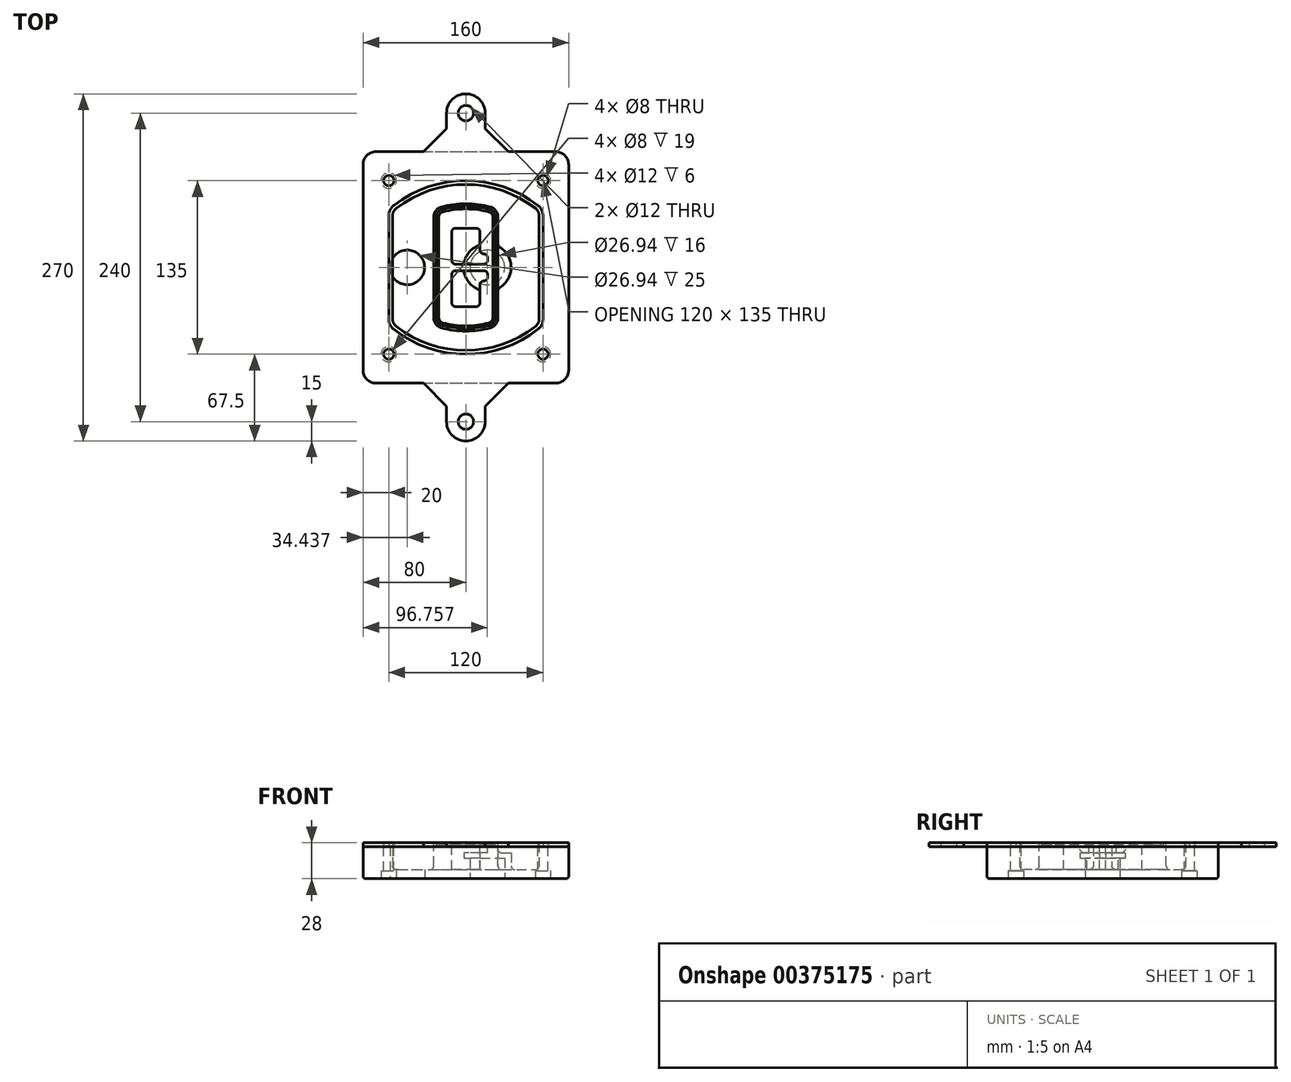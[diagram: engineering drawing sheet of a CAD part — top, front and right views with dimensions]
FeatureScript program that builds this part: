
annotation { "Feature Type Name" : "Feature", "Feature Type Description" : "" }
export const myFeature = defineFeature(function(context is Context, id is Id, definition is map)
    precondition{}
    {
        {
            var Q0;
            Q0=qCreatedBy(makeId("Top.planeOp"),FACE);
            var sketch = newSketch(context, id + "F0", { "sketchPlane" : qUnion([Q0])});
            skPoint(sketch, "E0.rect.middle", {"position": v(0, 0) * mm});
            skLineSegment(sketch, "E1.bottom", {"start": v(-70, -90) * mm, "end": v(70, -90) * mm});
            skLineSegment(sketch, "E1.top", {"start": v(-70, 90) * mm, "end": v(70, 90) * mm});
            skLineSegment(sketch, "E1.left", {"start": v(-80, -80) * mm, "end": v(-80, 80) * mm});
            skLineSegment(sketch, "E1.right", {"start": v(80, -80) * mm, "end": v(80, 80) * mm});
            skLineSegment(sketch, "E2", {"start": v(-80, 90) * mm, "end": v(80, -90) * mm, "construction": true});
            skLineSegment(sketch, "E3", {"start": v(80, 90) * mm, "end": v(-80, -90) * mm, "construction": true});
            skCircle(sketch, "E4", {"center": v(-60, 67.5) * mm, "radius": 4 * mm});
            skCircle(sketch, "E5", {"center": v(60, 67.5) * mm, "radius": 4 * mm});
            skCircle(sketch, "E6", {"center": v(60, -67.5) * mm, "radius": 4 * mm});
            skCircle(sketch, "E7", {"center": v(-60, -67.5) * mm, "radius": 4 * mm});
            skLineSegment(sketch, "E8", {"start": v(-60, 67.5) * mm, "end": v(60, 67.5) * mm, "construction": true});
            skLineSegment(sketch, "E9", {"start": v(60, 67.5) * mm, "end": v(60, -67.5) * mm, "construction": true});
            skLineSegment(sketch, "E10", {"start": v(60, -67.5) * mm, "end": v(-60, -67.5) * mm, "construction": true});
            skLineSegment(sketch, "E11", {"start": v(-60, -67.5) * mm, "end": v(-60, 67.5) * mm, "construction": true});
            skLineSegment(sketch, "E12", {"start": v(-60, 40.3) * mm, "end": v(-60, -40.3) * mm});
            skLineSegment(sketch, "E13", {"start": v(60, 40.3) * mm, "end": v(60, -40.3) * mm});
            skArc(sketch, "E14", {"start": v(56.15, 48.18) * mm, "mid": v(0, 67.5) * mm, "end": v(-56.15, 48.18) * mm});
            skArc(sketch, "E15", {"start": v(-56.15, -48.18) * mm, "mid": v(0, -67.5) * mm, "end": v(56.15, -48.18) * mm});
            skLineSegment(sketch, "E16", {"start": v(-60, 0) * mm, "end": v(60, 0) * mm, "construction": true});
            skPoint(sketch, "E17.visualSharp", {"position": v(-60, -45) * mm});
            skArc(sketch, "E17.filletArc", {"start": v(-60, -40.3) * mm, "mid": v(-58.99, -44.68) * mm, "end": v(-56.15, -48.18) * mm});
            skPoint(sketch, "E18.visualSharp", {"position": v(-60, 45) * mm});
            skArc(sketch, "E18.filletArc", {"start": v(-56.15, 48.18) * mm, "mid": v(-58.99, 44.68) * mm, "end": v(-60, 40.3) * mm});
            skPoint(sketch, "E19.visualSharp", {"position": v(60, 45) * mm});
            skArc(sketch, "E19.filletArc", {"start": v(60, 40.3) * mm, "mid": v(58.99, 44.68) * mm, "end": v(56.15, 48.18) * mm});
            skPoint(sketch, "E20.visualSharp", {"position": v(60, -45) * mm});
            skArc(sketch, "E20.filletArc", {"start": v(56.15, -48.18) * mm, "mid": v(58.99, -44.68) * mm, "end": v(60, -40.3) * mm});
            skPoint(sketch, "E21.visualSharp", {"position": v(-80, 90) * mm});
            skArc(sketch, "E21.filletArc", {"start": v(-70, 90) * mm, "mid": v(-77.07, 87.07) * mm, "end": v(-80, 80) * mm});
            skPoint(sketch, "E22.visualSharp", {"position": v(80, 90) * mm});
            skArc(sketch, "E22.filletArc", {"start": v(80, 80) * mm, "mid": v(77.07, 87.07) * mm, "end": v(70, 90) * mm});
            skPoint(sketch, "E23.visualSharp", {"position": v(80, -90) * mm});
            skArc(sketch, "E23.filletArc", {"start": v(70, -90) * mm, "mid": v(77.07, -87.07) * mm, "end": v(80, -80) * mm});
            skPoint(sketch, "E24.visualSharp", {"position": v(-80, -90) * mm});
            skArc(sketch, "E24.filletArc", {"start": v(-80, -80) * mm, "mid": v(-77.07, -87.07) * mm, "end": v(-70, -90) * mm});
            skArc(sketch, "E25.0", {"start": v(57, 40.3) * mm, "mid": v(56.3, 43.36) * mm, "end": v(54.3, 45.81) * mm});
            skLineSegment(sketch, "E25.1", {"start": v(57, 40.3) * mm, "end": v(57, -40.3) * mm});
            skArc(sketch, "E25.2", {"start": v(54.3, -45.81) * mm, "mid": v(56.3, -43.36) * mm, "end": v(57, -40.3) * mm});
            skArc(sketch, "E25.3", {"start": v(-54.3, -45.81) * mm, "mid": v(0, -64.5) * mm, "end": v(54.3, -45.81) * mm});
            skArc(sketch, "E25.4", {"start": v(-57, -40.3) * mm, "mid": v(-56.3, -43.36) * mm, "end": v(-54.3, -45.81) * mm});
            skArc(sketch, "E25.5", {"start": v(54.3, 45.81) * mm, "mid": v(0, 64.5) * mm, "end": v(-54.3, 45.81) * mm});
            skLineSegment(sketch, "E25.6", {"start": v(-57, 40.3) * mm, "end": v(-57, -40.3) * mm});
            skArc(sketch, "E25.7", {"start": v(-54.3, 45.81) * mm, "mid": v(-56.3, 43.36) * mm, "end": v(-57, 40.3) * mm});
            skArc(sketch, "E26.0", {"start": v(-58.62, 51.33) * mm, "mid": v(-62.58, 46.43) * mm, "end": v(-64, 40.3) * mm});
            skArc(sketch, "E26.1", {"start": v(58.62, 51.33) * mm, "mid": v(0, 71.5) * mm, "end": v(-58.62, 51.33) * mm});
            skArc(sketch, "E26.2", {"start": v(64, 40.3) * mm, "mid": v(62.58, 46.43) * mm, "end": v(58.62, 51.33) * mm});
            skLineSegment(sketch, "E26.3", {"start": v(64, 40.3) * mm, "end": v(64, -40.3) * mm});
            skArc(sketch, "E26.4", {"start": v(58.62, -51.33) * mm, "mid": v(62.58, -46.43) * mm, "end": v(64, -40.3) * mm});
            skLineSegment(sketch, "E26.5", {"start": v(-64, 40.3) * mm, "end": v(-64, -40.3) * mm});
            skArc(sketch, "E26.6", {"start": v(-58.62, -51.33) * mm, "mid": v(0, -71.5) * mm, "end": v(58.62, -51.33) * mm});
            skArc(sketch, "E26.7", {"start": v(-64, -40.3) * mm, "mid": v(-62.58, -46.43) * mm, "end": v(-58.62, -51.33) * mm});
            skSolve(sketch);
        }
        {
            var Q0;
            Q0=makeQuery(id+"F0.imprint","IMPRINT",FACE,{"disambiguationData":[TD([[makeQuery(id+"F0.imprint","IMPRINT",EDGE,{"derivedFrom":sQuery(id+"F0.wireOp",EDGE,"E1.bottom")}),1.0]])]});
            var Q1;
            Q1=makeQuery(id+"F0.imprint","IMPRINT",FACE,{"disambiguationData":[TD([[makeQuery(id+"F0.imprint","IMPRINT",EDGE,{"derivedFrom":sQuery(id+"F0.wireOp",EDGE,"E12")}),1.0]])]});
            var Q2;
            Q2=makeQuery(id+"F0.imprint","IMPRINT",FACE,{"disambiguationData":[TD([[makeQuery(id+"F0.imprint","IMPRINT",EDGE,{"derivedFrom":sQuery(id+"F0.wireOp",EDGE,"E25.0")}),1.0]])]});
            var Q3;
            Q3=makeQuery(id+"F0.imprint","IMPRINT",FACE,{"disambiguationData":[TD([[makeQuery(id+"F0.imprint","IMPRINT",EDGE,{"derivedFrom":sQuery(id+"F0.wireOp",EDGE,"E12")}),-1.0]])]});
            extrude(context, id + "F1", {"entities" : qUnion([Q0, Q1, Q2, Q3]), "oppositeDirection" : true, "depth" : 25 * mm});
        }
        {
            var Q0;
            Q0=makeQuery(id+"F0.imprint","IMPRINT",FACE,{"disambiguationData":[TD([[makeQuery(id+"F0.imprint","IMPRINT",EDGE,{"derivedFrom":sQuery(id+"F0.wireOp",EDGE,"E12")}),1.0]])]});
            extrude(context, id + "F2", {"entities" : qUnion([Q0]), "operationType" : NewBodyOperationType.ADD, "depth" : 3 * mm});
        }
        {
            var Q0;
            Q0=makeQuery(id+"F0.imprint","IMPRINT",FACE,{"disambiguationData":[TD([[makeQuery(id+"F0.imprint","IMPRINT",EDGE,{"derivedFrom":sQuery(id+"F0.wireOp",EDGE,"E25.0")}),1.0]])]});
            extrude(context, id + "F3", {"entities" : qUnion([Q0]), "operationType" : NewBodyOperationType.REMOVE, "oppositeDirection" : true, "depth" : 18 * mm});
        }
        {
            var Q0;
            Q0=makeQuery(id+"F2.opExtrude","CAP_FACE",FACE,{"disambiguationData":[OSD([sQuery(id+"F0.wireOp",EDGE,"E12"),sQuery(id+"F0.wireOp",EDGE,"E13"),sQuery(id+"F0.wireOp",EDGE,"E14"),sQuery(id+"F0.wireOp",EDGE,"E15"),sQuery(id+"F0.wireOp",EDGE,"E17.filletArc"),sQuery(id+"F0.wireOp",EDGE,"E18.filletArc"),sQuery(id+"F0.wireOp",EDGE,"E19.filletArc"),sQuery(id+"F0.wireOp",EDGE,"E20.filletArc"),sQuery(id+"F0.wireOp",EDGE,"E25.0"),sQuery(id+"F0.wireOp",EDGE,"E25.1"),sQuery(id+"F0.wireOp",EDGE,"E25.2"),sQuery(id+"F0.wireOp",EDGE,"E25.3"),sQuery(id+"F0.wireOp",EDGE,"E25.4"),sQuery(id+"F0.wireOp",EDGE,"E25.5"),sQuery(id+"F0.wireOp",EDGE,"E25.6"),sQuery(id+"F0.wireOp",EDGE,"E25.7")])],"isStart":false});
            var sketch = newSketch(context, id + "F4", { "sketchPlane" : qUnion([Q0])});
            skArc(sketch, "E27.0", {"start": v(-19.08, -46.97) * mm, "mid": v(0, -49.5) * mm, "end": v(19.08, -46.97) * mm});
            skArc(sketch, "E28.0", {"start": v(19.08, 46.97) * mm, "mid": v(0, 49.5) * mm, "end": v(-19.08, 46.97) * mm});
            skLineSegment(sketch, "E29", {"start": v(-25, 39.25) * mm, "end": v(-25, -39.25) * mm});
            skLineSegment(sketch, "E30", {"start": v(25, 39.25) * mm, "end": v(25, -39.25) * mm});
            skLineSegment(sketch, "E31", {"start": v(-25, 45.1) * mm, "end": v(25, 45.1) * mm, "construction": true});
            skLineSegment(sketch, "E32", {"start": v(-25, -45.1) * mm, "end": v(25, -45.1) * mm, "construction": true});
            skPoint(sketch, "E33.visualSharp", {"position": v(-25, 45.1) * mm});
            skArc(sketch, "E33.filletArc", {"start": v(-19.08, 46.97) * mm, "mid": v(-23.35, 44.11) * mm, "end": v(-25, 39.25) * mm});
            skPoint(sketch, "E34.visualSharp", {"position": v(25, 45.1) * mm});
            skArc(sketch, "E34.filletArc", {"start": v(25, 39.25) * mm, "mid": v(23.35, 44.11) * mm, "end": v(19.08, 46.97) * mm});
            skPoint(sketch, "E35.visualSharp", {"position": v(25, -45.1) * mm});
            skArc(sketch, "E35.filletArc", {"start": v(19.08, -46.97) * mm, "mid": v(23.35, -44.11) * mm, "end": v(25, -39.25) * mm});
            skPoint(sketch, "E36.visualSharp", {"position": v(-25, -45.1) * mm});
            skArc(sketch, "E36.filletArc", {"start": v(-25, -39.25) * mm, "mid": v(-23.35, -44.11) * mm, "end": v(-19.08, -46.97) * mm});
            skArc(sketch, "E37.0", {"start": v(54.3, 45.81) * mm, "mid": v(0, 64.5) * mm, "end": v(-54.3, 45.81) * mm});
            skArc(sketch, "E37.1", {"start": v(-54.3, 45.81) * mm, "mid": v(-56.3, 43.36) * mm, "end": v(-57, 40.3) * mm});
            skLineSegment(sketch, "E37.2", {"start": v(-57, 40.3) * mm, "end": v(-57, -40.3) * mm});
            skArc(sketch, "E37.3", {"start": v(-57, -40.3) * mm, "mid": v(-56.3, -43.36) * mm, "end": v(-54.3, -45.81) * mm});
            skArc(sketch, "E37.4", {"start": v(-54.3, -45.81) * mm, "mid": v(0, -64.5) * mm, "end": v(54.3, -45.81) * mm});
            skArc(sketch, "E37.5", {"start": v(54.3, -45.81) * mm, "mid": v(56.3, -43.36) * mm, "end": v(57, -40.3) * mm});
            skLineSegment(sketch, "E37.6", {"start": v(57, 40.3) * mm, "end": v(57, -40.3) * mm});
            skArc(sketch, "E37.7", {"start": v(57, 40.3) * mm, "mid": v(56.3, 43.36) * mm, "end": v(54.3, 45.81) * mm});
            skLineSegment(sketch, "E38.0", {"start": v(23, 39.25) * mm, "end": v(23, -39.25) * mm});
            skArc(sketch, "E38.1", {"start": v(18.56, -45.04) * mm, "mid": v(21.76, -42.9) * mm, "end": v(23, -39.25) * mm});
            skArc(sketch, "E38.2", {"start": v(-18.56, -45.04) * mm, "mid": v(0, -47.5) * mm, "end": v(18.56, -45.04) * mm});
            skArc(sketch, "E38.3", {"start": v(-23, -39.25) * mm, "mid": v(-21.76, -42.9) * mm, "end": v(-18.56, -45.04) * mm});
            skLineSegment(sketch, "E38.4", {"start": v(-23, 39.25) * mm, "end": v(-23, -39.25) * mm});
            skArc(sketch, "E38.5", {"start": v(23, 39.25) * mm, "mid": v(21.76, 42.9) * mm, "end": v(18.56, 45.04) * mm});
            skArc(sketch, "E38.6", {"start": v(-18.56, 45.04) * mm, "mid": v(-21.76, 42.9) * mm, "end": v(-23, 39.25) * mm});
            skArc(sketch, "E38.7", {"start": v(18.56, 45.04) * mm, "mid": v(0, 47.5) * mm, "end": v(-18.56, 45.04) * mm});
            skArc(sketch, "E39.0", {"start": v(21, 39.25) * mm, "mid": v(20.18, 41.68) * mm, "end": v(18.04, 43.1) * mm});
            skLineSegment(sketch, "E39.1", {"start": v(21, 39.25) * mm, "end": v(21, -39.25) * mm});
            skArc(sketch, "E39.2", {"start": v(18.04, -43.1) * mm, "mid": v(20.18, -41.68) * mm, "end": v(21, -39.25) * mm});
            skArc(sketch, "E39.3", {"start": v(-18.04, -43.1) * mm, "mid": v(0, -45.5) * mm, "end": v(18.04, -43.1) * mm});
            skArc(sketch, "E39.4", {"start": v(-21, -39.25) * mm, "mid": v(-20.18, -41.68) * mm, "end": v(-18.04, -43.1) * mm});
            skArc(sketch, "E39.5", {"start": v(18.04, 43.1) * mm, "mid": v(0, 45.5) * mm, "end": v(-18.04, 43.1) * mm});
            skLineSegment(sketch, "E39.6", {"start": v(-21, 39.25) * mm, "end": v(-21, -39.25) * mm});
            skArc(sketch, "E39.7", {"start": v(-18.04, 43.1) * mm, "mid": v(-20.18, 41.68) * mm, "end": v(-21, 39.25) * mm});
            skLineSegment(sketch, "E40", {"start": v(-25, 0) * mm, "end": v(25, 0) * mm, "construction": true});
            skLineSegment(sketch, "E41", {"start": v(-11, 5.5) * mm, "end": v(-11, 27.5) * mm});
            skLineSegment(sketch, "E42", {"start": v(-8, 30.5) * mm, "end": v(8, 30.5) * mm});
            skLineSegment(sketch, "E43", {"start": v(11, 27.5) * mm, "end": v(11, 13.5) * mm});
            skLineSegment(sketch, "E44", {"start": v(14, 10.5) * mm, "end": v(14, 10.5) * mm});
            skLineSegment(sketch, "E45", {"start": v(17, 7.5) * mm, "end": v(17, 5.5) * mm});
            skLineSegment(sketch, "E46", {"start": v(14, 2.5) * mm, "end": v(-8, 2.5) * mm});
            skPoint(sketch, "E47.visualSharp", {"position": v(-11, 30.5) * mm});
            skArc(sketch, "E47.filletArc", {"start": v(-8, 30.5) * mm, "mid": v(-10.12, 29.62) * mm, "end": v(-11, 27.5) * mm});
            skPoint(sketch, "E48.visualSharp", {"position": v(11, 30.5) * mm});
            skArc(sketch, "E48.filletArc", {"start": v(11, 27.5) * mm, "mid": v(10.12, 29.62) * mm, "end": v(8, 30.5) * mm});
            skPoint(sketch, "E49.visualSharp", {"position": v(11, 10.5) * mm});
            skArc(sketch, "E49.filletArc", {"start": v(11, 13.5) * mm, "mid": v(11.88, 11.38) * mm, "end": v(14, 10.5) * mm});
            skPoint(sketch, "E50.visualSharp", {"position": v(17, 10.5) * mm});
            skArc(sketch, "E50.filletArc", {"start": v(17, 7.5) * mm, "mid": v(16.12, 9.62) * mm, "end": v(14, 10.5) * mm});
            skPoint(sketch, "E51.visualSharp", {"position": v(17, 2.5) * mm});
            skArc(sketch, "E51.filletArc", {"start": v(14, 2.5) * mm, "mid": v(16.12, 3.38) * mm, "end": v(17, 5.5) * mm});
            skPoint(sketch, "E52.visualSharp", {"position": v(-11, 2.5) * mm});
            skArc(sketch, "E52.filletArc", {"start": v(-11, 5.5) * mm, "mid": v(-10.12, 3.38) * mm, "end": v(-8, 2.5) * mm});
            skLineSegment(sketch, "E53.0.MirrorCS", {"start": v(14, -2.5) * mm, "end": v(-8, -2.5) * mm});
            skArc(sketch, "E54.0.MirrorCS", {"start": v(-11, -5.5) * mm, "mid": v(-10.12, -3.38) * mm, "end": v(-8, -2.5) * mm});
            skLineSegment(sketch, "E55.0.MirrorCS", {"start": v(-11, -5.5) * mm, "end": v(-11, -27.5) * mm});
            skArc(sketch, "E56.0.MirrorCS", {"start": v(-8, -30.5) * mm, "mid": v(-10.12, -29.62) * mm, "end": v(-11, -27.5) * mm});
            skLineSegment(sketch, "E57.0.MirrorCS", {"start": v(-8, -30.5) * mm, "end": v(8, -30.5) * mm});
            skArc(sketch, "E58.0.MirrorCS", {"start": v(11, -27.5) * mm, "mid": v(10.12, -29.62) * mm, "end": v(8, -30.5) * mm});
            skLineSegment(sketch, "E59.0.MirrorCS", {"start": v(11, -27.5) * mm, "end": v(11, -13.5) * mm});
            skArc(sketch, "E60.0.MirrorCS", {"start": v(11, -13.5) * mm, "mid": v(11.88, -11.38) * mm, "end": v(14, -10.5) * mm});
            skArc(sketch, "E61.0.MirrorCS", {"start": v(17, -7.5) * mm, "mid": v(16.12, -9.62) * mm, "end": v(14, -10.5) * mm});
            skLineSegment(sketch, "E62.0.MirrorCS", {"start": v(17, -7.5) * mm, "end": v(17, -5.5) * mm});
            skArc(sketch, "E63.0.MirrorCS", {"start": v(14, -2.5) * mm, "mid": v(16.12, -3.38) * mm, "end": v(17, -5.5) * mm});
            skSolve(sketch);
        }
        {
            var Q0;
            Q0=makeQuery(id+"F4.imprint","IMPRINT",FACE,{"disambiguationData":[TD([[makeQuery(id+"F4.imprint","IMPRINT",EDGE,{"derivedFrom":sQuery(id+"F4.wireOp",EDGE,"E27.0")}),1.0]])]});
            var Q1;
            Q1=makeQuery(id+"F4.imprint","IMPRINT",FACE,{"disambiguationData":[TD([[makeQuery(id+"F4.imprint","IMPRINT",EDGE,{"derivedFrom":sQuery(id+"F4.wireOp",EDGE,"E38.0")}),-1.0]])]});
            var Q2;
            Q2=makeQuery(id+"F4.imprint","IMPRINT",FACE,{"disambiguationData":[TD([[makeQuery(id+"F4.imprint","IMPRINT",EDGE,{"derivedFrom":sQuery(id+"F4.wireOp",EDGE,"E39.0")}),1.0]])]});
            extrude(context, id + "F5", {"entities" : qUnion([Q0, Q1, Q2]), "operationType" : NewBodyOperationType.ADD, "endBound" : BoundingType.UP_TO_NEXT, "oppositeDirection" : true, "depth" : 25 * mm});
        }
        {
            var Q0;
            Q0=makeQuery(id+"F4.imprint","IMPRINT",FACE,{"disambiguationData":[TD([[makeQuery(id+"F4.imprint","IMPRINT",EDGE,{"derivedFrom":sQuery(id+"F4.wireOp",EDGE,"E38.0")}),-1.0]])]});
            extrude(context, id + "F6", {"entities" : qUnion([Q0]), "operationType" : NewBodyOperationType.REMOVE, "oppositeDirection" : true, "depth" : 2 * mm});
        }
        {
            var Q0;
            Q0=makeQuery(id+"F1.opExtrude","CAP_FACE",FACE,{"disambiguationData":[OSD([sQuery(id+"F0.wireOp",EDGE,"E1.bottom"),sQuery(id+"F0.wireOp",EDGE,"E1.top"),sQuery(id+"F0.wireOp",EDGE,"E1.left"),sQuery(id+"F0.wireOp",EDGE,"E1.right"),sQuery(id+"F0.wireOp",EDGE,"E4"),sQuery(id+"F0.wireOp",EDGE,"E5"),sQuery(id+"F0.wireOp",EDGE,"E6"),sQuery(id+"F0.wireOp",EDGE,"E7"),sQuery(id+"F0.wireOp",EDGE,"E21.filletArc"),sQuery(id+"F0.wireOp",EDGE,"E22.filletArc"),sQuery(id+"F0.wireOp",EDGE,"E23.filletArc"),sQuery(id+"F0.wireOp",EDGE,"E24.filletArc")])],"isStart":false});
            var sketch = newSketch(context, id + "F7", { "sketchPlane" : qUnion([Q0])});
            skCircle(sketch, "E64", {"center": v(16.76, 0) * mm, "radius": 13.47 * mm});
            skCircle(sketch, "E65", {"center": v(-45.56, 0) * mm, "radius": 13.47 * mm});
            skLineSegment(sketch, "E66", {"start": v(80, 0) * mm, "end": v(-80, 0) * mm});
            skCircle(sketch, "E67", {"center": v(16.76, 0) * mm, "radius": 18.47 * mm});
            skCircle(sketch, "E68", {"center": v(60, -67.5) * mm, "radius": 6 * mm});
            skCircle(sketch, "E69", {"center": v(-60, -67.5) * mm, "radius": 6 * mm});
            skCircle(sketch, "E70", {"center": v(-60, 67.5) * mm, "radius": 6 * mm});
            skCircle(sketch, "E71", {"center": v(60, 67.5) * mm, "radius": 6 * mm});
            skSolve(sketch);
        }
        {
            var Q0;
            {var subQ1=sQuery(id+"F7.wireOp",EDGE,"E66");var subQ4=sQuery(id+"F7.wireOp",EDGE,"E64");var subQ6=makeQuery(id+"F7.imprint","INTERSECT",VERTEX,{"disambiguationData":[OD(0.0)],"derivedFrom":[subQ4,subQ1]});Q0=makeQuery(id+"F7.imprint","IMPRINT",FACE,{"disambiguationData":[TD([[makeQuery(id+"F7.imprint","IMPRINT",EDGE,{"disambiguationData":[TD([[subQ6,-1.0]])],"derivedFrom":subQ4}),-1.0]])]});}
            var Q1;
            {var subQ0=sQuery(id+"F7.wireOp",EDGE,"E66");var subQ1=sQuery(id+"F7.wireOp",EDGE,"E64");var subQ3=makeQuery(id+"F7.imprint","INTERSECT",VERTEX,{"disambiguationData":[OD(0.0)],"derivedFrom":[subQ1,subQ0]});Q1=makeQuery(id+"F7.imprint","IMPRINT",FACE,{"disambiguationData":[TD([[makeQuery(id+"F7.imprint","IMPRINT",EDGE,{"disambiguationData":[TD([[subQ3,-1.0]])],"derivedFrom":subQ1}),1.0]])]});}
            var Q2;
            {var subQ0=sQuery(id+"F7.wireOp",EDGE,"E66");var subQ1=sQuery(id+"F7.wireOp",EDGE,"E64");var subQ3=makeQuery(id+"F7.imprint","INTERSECT",VERTEX,{"disambiguationData":[OD(0.0)],"derivedFrom":[subQ1,subQ0]});Q2=makeQuery(id+"F7.imprint","IMPRINT",FACE,{"disambiguationData":[TD([[makeQuery(id+"F7.imprint","IMPRINT",EDGE,{"disambiguationData":[TD([[subQ3,1.0]])],"derivedFrom":subQ1}),1.0]])]});}
            var Q3;
            {var subQ1=sQuery(id+"F7.wireOp",EDGE,"E66");var subQ4=sQuery(id+"F7.wireOp",EDGE,"E64");var subQ6=makeQuery(id+"F7.imprint","INTERSECT",VERTEX,{"disambiguationData":[OD(0.0)],"derivedFrom":[subQ4,subQ1]});Q3=makeQuery(id+"F7.imprint","IMPRINT",FACE,{"disambiguationData":[TD([[makeQuery(id+"F7.imprint","IMPRINT",EDGE,{"disambiguationData":[TD([[subQ6,1.0]])],"derivedFrom":subQ4}),-1.0]])]});}
            extrude(context, id + "F8", {"entities" : qUnion([Q0, Q1, Q2, Q3]), "operationType" : NewBodyOperationType.ADD, "oppositeDirection" : true, "depth" : 20 * mm});
        }
        {
            var Q0;
            {var subQ0=sQuery(id+"F7.wireOp",EDGE,"E66");var subQ1=sQuery(id+"F7.wireOp",EDGE,"E64");var subQ3=makeQuery(id+"F7.imprint","INTERSECT",VERTEX,{"disambiguationData":[OD(0.0)],"derivedFrom":[subQ1,subQ0]});Q0=makeQuery(id+"F7.imprint","IMPRINT",FACE,{"disambiguationData":[TD([[makeQuery(id+"F7.imprint","IMPRINT",EDGE,{"disambiguationData":[TD([[subQ3,-1.0]])],"derivedFrom":subQ1}),1.0]])]});}
            var Q1;
            {var subQ0=sQuery(id+"F7.wireOp",EDGE,"E66");var subQ1=sQuery(id+"F7.wireOp",EDGE,"E64");var subQ3=makeQuery(id+"F7.imprint","INTERSECT",VERTEX,{"disambiguationData":[OD(0.0)],"derivedFrom":[subQ1,subQ0]});Q1=makeQuery(id+"F7.imprint","IMPRINT",FACE,{"disambiguationData":[TD([[makeQuery(id+"F7.imprint","IMPRINT",EDGE,{"disambiguationData":[TD([[subQ3,1.0]])],"derivedFrom":subQ1}),1.0]])]});}
            extrude(context, id + "F9", {"entities" : qUnion([Q0, Q1]), "operationType" : NewBodyOperationType.REMOVE, "oppositeDirection" : true, "depth" : 16 * mm});
        }
        {
            var Q0;
            {var subQ0=sQuery(id+"F7.wireOp",EDGE,"E66");var subQ1=sQuery(id+"F7.wireOp",EDGE,"E65");var subQ3=makeQuery(id+"F7.imprint","INTERSECT",VERTEX,{"disambiguationData":[OD(0.0)],"derivedFrom":[subQ1,subQ0]});Q0=makeQuery(id+"F7.imprint","IMPRINT",FACE,{"disambiguationData":[TD([[makeQuery(id+"F7.imprint","IMPRINT",EDGE,{"disambiguationData":[TD([[subQ3,-1.0]])],"derivedFrom":subQ1}),1.0]])]});}
            var Q1;
            {var subQ0=sQuery(id+"F7.wireOp",EDGE,"E66");var subQ1=sQuery(id+"F7.wireOp",EDGE,"E65");var subQ3=makeQuery(id+"F7.imprint","INTERSECT",VERTEX,{"disambiguationData":[OD(0.0)],"derivedFrom":[subQ1,subQ0]});Q1=makeQuery(id+"F7.imprint","IMPRINT",FACE,{"disambiguationData":[TD([[makeQuery(id+"F7.imprint","IMPRINT",EDGE,{"disambiguationData":[TD([[subQ3,1.0]])],"derivedFrom":subQ1}),1.0]])]});}
            extrude(context, id + "F10", {"entities" : qUnion([Q0, Q1]), "operationType" : NewBodyOperationType.REMOVE, "oppositeDirection" : true, "depth" : 25 * mm});
        }
        {
            var Q0;
            Q0=makeQuery(id+"F7.imprint","IMPRINT",FACE,{"disambiguationData":[TD([[makeQuery(id+"F7.imprint","IMPRINT",EDGE,{"derivedFrom":sQuery(id+"F7.wireOp",EDGE,"E68")}),1.0]])]});
            var Q1;
            Q1=makeQuery(id+"F7.imprint","IMPRINT",FACE,{"disambiguationData":[TD([[makeQuery(id+"F7.imprint","IMPRINT",EDGE,{"derivedFrom":makeQuery(id+"F1.opExtrude","CAP_EDGE",EDGE,{"disambiguationData":[OSD([sQuery(id+"F0.wireOp",EDGE,"E5")])],"isStart":false})}),-1.0]])]});
            var Q2;
            Q2=makeQuery(id+"F7.imprint","IMPRINT",FACE,{"disambiguationData":[TD([[makeQuery(id+"F7.imprint","IMPRINT",EDGE,{"derivedFrom":sQuery(id+"F7.wireOp",EDGE,"E69")}),1.0]])]});
            var Q3;
            Q3=makeQuery(id+"F7.imprint","IMPRINT",FACE,{"disambiguationData":[TD([[makeQuery(id+"F7.imprint","IMPRINT",EDGE,{"derivedFrom":makeQuery(id+"F1.opExtrude","CAP_EDGE",EDGE,{"disambiguationData":[OSD([sQuery(id+"F0.wireOp",EDGE,"E4")])],"isStart":false})}),-1.0]])]});
            var Q4;
            Q4=makeQuery(id+"F7.imprint","IMPRINT",FACE,{"disambiguationData":[TD([[makeQuery(id+"F7.imprint","IMPRINT",EDGE,{"derivedFrom":sQuery(id+"F7.wireOp",EDGE,"E70")}),1.0]])]});
            var Q5;
            Q5=makeQuery(id+"F7.imprint","IMPRINT",FACE,{"disambiguationData":[TD([[makeQuery(id+"F7.imprint","IMPRINT",EDGE,{"derivedFrom":makeQuery(id+"F1.opExtrude","CAP_EDGE",EDGE,{"disambiguationData":[OSD([sQuery(id+"F0.wireOp",EDGE,"E7")])],"isStart":false})}),-1.0]])]});
            var Q6;
            Q6=makeQuery(id+"F7.imprint","IMPRINT",FACE,{"disambiguationData":[TD([[makeQuery(id+"F7.imprint","IMPRINT",EDGE,{"derivedFrom":sQuery(id+"F7.wireOp",EDGE,"E71")}),1.0]])]});
            var Q7;
            Q7=makeQuery(id+"F7.imprint","IMPRINT",FACE,{"disambiguationData":[TD([[makeQuery(id+"F7.imprint","IMPRINT",EDGE,{"derivedFrom":makeQuery(id+"F1.opExtrude","CAP_EDGE",EDGE,{"disambiguationData":[OSD([sQuery(id+"F0.wireOp",EDGE,"E6")])],"isStart":false})}),-1.0]])]});
            extrude(context, id + "F11", {"entities" : qUnion([Q0, Q1, Q2, Q3, Q4, Q5, Q6, Q7]), "operationType" : NewBodyOperationType.REMOVE, "oppositeDirection" : true, "depth" : 6 * mm});
        }
        {
            var Q0;
            Q0=makeQuery(id+"F9.boolean.opBoolean","COPY",FACE,{"derivedFrom":makeQuery(id+"F9.opExtrude","CAP_FACE",FACE,{"disambiguationData":[OSD([sQuery(id+"F7.wireOp",EDGE,"E64")])],"isStart":false})});
            var sketch = newSketch(context, id + "F12", { "sketchPlane" : qUnion([Q0])});
            skArc(sketch, "E72.0", {"start": v(11, 17.55) * mm, "mid": v(2.57, 11.82) * mm, "end": v(-1.54, 2.5) * mm});
            skArc(sketch, "E72.1", {"start": v(-1.54, -2.5) * mm, "mid": v(2.57, -11.82) * mm, "end": v(11, -17.55) * mm});
            skLineSegment(sketch, "E73", {"start": v(-1.54, -2.5) * mm, "end": v(14, -2.5) * mm});
            skLineSegment(sketch, "E74.0", {"start": v(14, 2.5) * mm, "end": v(-1.54, 2.5) * mm});
            skArc(sketch, "E74.1", {"start": v(14, 2.5) * mm, "mid": v(16.12, 3.38) * mm, "end": v(17, 5.5) * mm});
            skLineSegment(sketch, "E74.2", {"start": v(17, 7.5) * mm, "end": v(17, 5.5) * mm});
            skArc(sketch, "E74.3", {"start": v(17, 7.5) * mm, "mid": v(16.12, 9.62) * mm, "end": v(14, 10.5) * mm});
            skArc(sketch, "E74.4", {"start": v(11, 13.5) * mm, "mid": v(11.88, 11.38) * mm, "end": v(14, 10.5) * mm});
            skLineSegment(sketch, "E74.5", {"start": v(11, 17.55) * mm, "end": v(11, 13.5) * mm});
            skLineSegment(sketch, "E74.7", {"start": v(14, -2.5) * mm, "end": v(-1.54, -2.5) * mm});
            skArc(sketch, "E74.8", {"start": v(14, -2.5) * mm, "mid": v(16.12, -3.38) * mm, "end": v(17, -5.5) * mm});
            skLineSegment(sketch, "E74.9", {"start": v(17, -7.5) * mm, "end": v(17, -5.5) * mm});
            skArc(sketch, "E74.10", {"start": v(17, -7.5) * mm, "mid": v(16.12, -9.62) * mm, "end": v(14, -10.5) * mm});
            skArc(sketch, "E74.11", {"start": v(11, -13.5) * mm, "mid": v(11.88, -11.38) * mm, "end": v(14, -10.5) * mm});
            skLineSegment(sketch, "E74.12", {"start": v(11, -17.55) * mm, "end": v(11, -13.5) * mm});
            skPoint(sketch, "E75.orphan", {"position": v(11, -27.5) * mm});
            skPoint(sketch, "E76.orphan", {"position": v(-8, -2.5) * mm});
            skPoint(sketch, "E77.orphan", {"position": v(-8, 2.5) * mm});
            skPoint(sketch, "E78.orphan", {"position": v(11, 27.5) * mm});
            skSolve(sketch);
        }
        {
            var Q0;
            {var subQ7=sQuery(id+"F12.wireOp",EDGE,"E72.0");var subQ14=sQuery(id+"F12.wireOp",EDGE,"E72.1");var subQ16=sQuery(id+"F12.wireOp",EDGE,"E74.1");var subQ18=sQuery(id+"F12.wireOp",EDGE,"E74.8");Q0=qUnion([makeQuery(id+"F12.imprint","IMPRINT",FACE,{"disambiguationData":[TD([[makeQuery(id+"F12.imprint","IMPRINT",EDGE,{"derivedFrom":subQ7}),1.0]])]}),makeQuery(id+"F12.imprint","IMPRINT",FACE,{"disambiguationData":[TD([[makeQuery(id+"F12.imprint","IMPRINT",EDGE,{"derivedFrom":subQ14}),1.0]])]}),makeQuery(id+"F12.imprint","IMPRINT",FACE,{"disambiguationData":[TD([[makeQuery(id+"F12.imprint","IMPRINT",EDGE,{"derivedFrom":subQ16}),1.0]])]}),makeQuery(id+"F12.imprint","IMPRINT",FACE,{"disambiguationData":[TD([[makeQuery(id+"F12.imprint","IMPRINT",EDGE,{"derivedFrom":subQ18}),-1.0]])]})]);}
            var Q1;
            Q1=makeQuery(id+"F5.boolean.opBoolean","SPLIT",FACE,{"disambiguationData":[TD([makeQuery(id+"F5.opExtrude","SWEPT_FACE",FACE,{"disambiguationData":[OSD([sQuery(id+"F4.wireOp",EDGE,"E41")])]})])],"derivedFrom":makeQuery(id+"F3.boolean.opBoolean","COPY",FACE,{"derivedFrom":makeQuery(id+"F3.opExtrude","CAP_FACE",FACE,{"disambiguationData":[OSD([sQuery(id+"F0.wireOp",EDGE,"E25.0"),sQuery(id+"F0.wireOp",EDGE,"E25.1"),sQuery(id+"F0.wireOp",EDGE,"E25.2"),sQuery(id+"F0.wireOp",EDGE,"E25.3"),sQuery(id+"F0.wireOp",EDGE,"E25.4"),sQuery(id+"F0.wireOp",EDGE,"E25.5"),sQuery(id+"F0.wireOp",EDGE,"E25.6"),sQuery(id+"F0.wireOp",EDGE,"E25.7")])],"isStart":false})})});
            extrude(context, id + "F13", {"entities" : qUnion([Q0]), "operationType" : NewBodyOperationType.REMOVE, "endBound" : BoundingType.UP_TO_SURFACE, "endBoundEntityFace" : qUnion([Q1]), "depth" : 25 * mm});
        }
        {
            var Q0;
            Q0=makeQuery(id+"F3.boolean.opBoolean","COPY",EDGE,{"derivedFrom":makeQuery(id+"F3.opExtrude","CAP_EDGE",EDGE,{"disambiguationData":[OSD([sQuery(id+"F0.wireOp",EDGE,"E25.6")])],"isStart":false})});
            var Q1;
            Q1=makeQuery(id+"F8.boolean.opBoolean","INTERSECT",EDGE,{"derivedFrom":[makeQuery(id+"F5.opExtrude","SWEPT_FACE",FACE,{"disambiguationData":[OSD([sQuery(id+"F4.wireOp",EDGE,"E30")])]}),makeQuery(id+"F8.opExtrude","CAP_FACE",FACE,{"disambiguationData":[OSD([sQuery(id+"F7.wireOp",EDGE,"E67")])],"isStart":false})]});
            var Q2;
            Q2=makeQuery(id+"F8.boolean.opBoolean","INTERSECT",EDGE,{"disambiguationData":[OD(1.0)],"derivedFrom":[makeQuery(id+"F5.opExtrude","SWEPT_FACE",FACE,{"disambiguationData":[OSD([sQuery(id+"F4.wireOp",EDGE,"E30")])]}),makeQuery(id+"F8.opExtrude","SWEPT_FACE",FACE,{"disambiguationData":[OSD([sQuery(id+"F7.wireOp",EDGE,"E67")])]})]});
            var Q3;
            {var subQ0=sQuery(id+"F4.wireOp",EDGE,"E30");Q3=makeQuery(id+"F8.boolean.opBoolean","SPLIT",EDGE,{"disambiguationData":[TD([makeQuery(id+"F5.opExtrude","SWEPT_FACE",FACE,{"disambiguationData":[OSD([sQuery(id+"F4.wireOp",EDGE,"E35.filletArc")])]})])],"derivedFrom":makeQuery(id+"F5.opExtrude","CAP_EDGE",EDGE,{"disambiguationData":[OSD([subQ0])],"isStart":false})});}
            var Q4;
            {var subQ0=sQuery(id+"F0.wireOp",EDGE,"E25.7");var subQ1=sQuery(id+"F0.wireOp",EDGE,"E25.1");var subQ2=sQuery(id+"F0.wireOp",EDGE,"E25.6");var subQ3=sQuery(id+"F0.wireOp",EDGE,"E25.5");var subQ4=sQuery(id+"F0.wireOp",EDGE,"E25.4");var subQ5=sQuery(id+"F0.wireOp",EDGE,"E25.0");var subQ6=sQuery(id+"F0.wireOp",EDGE,"E25.2");var subQ7=sQuery(id+"F0.wireOp",EDGE,"E25.3");Q4=makeQuery(id+"F8.boolean.opBoolean","INTERSECT",EDGE,{"derivedFrom":[makeQuery(id+"F5.boolean.opBoolean","SPLIT",FACE,{"disambiguationData":[TD([makeQuery(id+"F2.opExtrude","SWEPT_FACE",FACE,{"disambiguationData":[OSD([subQ5])]})])],"derivedFrom":makeQuery(id+"F3.boolean.opBoolean","COPY",FACE,{"derivedFrom":makeQuery(id+"F3.opExtrude","CAP_FACE",FACE,{"disambiguationData":[OSD([subQ5,subQ1,subQ6,subQ7,subQ4,subQ3,subQ2,subQ0])],"isStart":false})})}),makeQuery(id+"F8.opExtrude","SWEPT_FACE",FACE,{"disambiguationData":[OSD([sQuery(id+"F7.wireOp",EDGE,"E67")])]})]});}
            var Q5;
            Q5=makeQuery(id+"F8.boolean.opBoolean","INTERSECT",EDGE,{"disambiguationData":[OD(0.0)],"derivedFrom":[makeQuery(id+"F5.opExtrude","SWEPT_FACE",FACE,{"disambiguationData":[OSD([sQuery(id+"F4.wireOp",EDGE,"E30")])]}),makeQuery(id+"F8.opExtrude","SWEPT_FACE",FACE,{"disambiguationData":[OSD([sQuery(id+"F7.wireOp",EDGE,"E67")])]})]});
            fillet(context, id + "F14", {"entities" : qUnion([Q0, Q1, Q2, Q3, Q4, Q5]), "radius" : 3 * mm, "tangentPropagation" : true, "allowEdgeOverflow" : false});
        }
        {
            var Q0;
            Q0=makeQuery(id+"F1.opExtrude","CAP_EDGE",EDGE,{"disambiguationData":[OSD([sQuery(id+"F0.wireOp",EDGE,"E1.bottom")])],"isStart":false});
            fillet(context, id + "F15", {"entities" : qUnion([Q0]), "radius" : 2 * mm, "tangentPropagation" : true, "allowEdgeOverflow" : false});
        }
        {
            var Q0;
            {var subQ0=sQuery(id+"F0.wireOp",EDGE,"E21.filletArc");var subQ1=sQuery(id+"F0.wireOp",EDGE,"E7");var subQ2=sQuery(id+"F0.wireOp",EDGE,"E6");var subQ3=sQuery(id+"F0.wireOp",EDGE,"E5");var subQ4=sQuery(id+"F0.wireOp",EDGE,"E4");var subQ5=sQuery(id+"F0.wireOp",EDGE,"E22.filletArc");var subQ6=sQuery(id+"F0.wireOp",EDGE,"E1.bottom");var subQ7=sQuery(id+"F0.wireOp",EDGE,"E1.right");var subQ8=sQuery(id+"F0.wireOp",EDGE,"E1.top");var subQ9=sQuery(id+"F0.wireOp",EDGE,"E1.left");var subQ10=sQuery(id+"F0.wireOp",EDGE,"E23.filletArc");var subQ11=sQuery(id+"F0.wireOp",EDGE,"E24.filletArc");Q0=makeQuery(id+"F2.boolean.opBoolean","SPLIT",FACE,{"disambiguationData":[TD([makeQuery(id+"F1.opExtrude","SWEPT_FACE",FACE,{"disambiguationData":[OSD([subQ6])]})])],"derivedFrom":makeQuery(id+"F1.opExtrude","CAP_FACE",FACE,{"disambiguationData":[OSD([subQ6,subQ8,subQ9,subQ7,subQ4,subQ3,subQ2,subQ1,subQ0,subQ5,subQ10,subQ11])],"isStart":true})});}
            var sketch = newSketch(context, id + "F16", { "sketchPlane" : qUnion([Q0])});
            skLineSegment(sketch, "E79.0", {"start": v(-70, 90) * mm, "end": v(70, 90) * mm});
            skLineSegment(sketch, "E79.1", {"start": v(80, -80) * mm, "end": v(80, 80) * mm});
            skArc(sketch, "E79.2", {"start": v(80, 80) * mm, "mid": v(77.07, 87.07) * mm, "end": v(70, 90) * mm});
            skArc(sketch, "E79.3", {"start": v(70, -90) * mm, "mid": v(77.07, -87.07) * mm, "end": v(80, -80) * mm});
            skLineSegment(sketch, "E79.4", {"start": v(-70, -90) * mm, "end": v(70, -90) * mm});
            skArc(sketch, "E79.5", {"start": v(-80, -80) * mm, "mid": v(-77.07, -87.07) * mm, "end": v(-70, -90) * mm});
            skLineSegment(sketch, "E79.6", {"start": v(-80, -80) * mm, "end": v(-80, 80) * mm});
            skArc(sketch, "E79.7", {"start": v(-70, 90) * mm, "mid": v(-77.07, 87.07) * mm, "end": v(-80, 80) * mm});
            skArc(sketch, "E79.8", {"start": v(56.15, 48.18) * mm, "mid": v(0, 67.5) * mm, "end": v(-56.15, 48.18) * mm});
            skArc(sketch, "E79.9", {"start": v(60, 40.3) * mm, "mid": v(58.99, 44.68) * mm, "end": v(56.15, 48.18) * mm});
            skLineSegment(sketch, "E79.10", {"start": v(60, 40.3) * mm, "end": v(60, -40.3) * mm});
            skArc(sketch, "E79.11", {"start": v(56.15, -48.18) * mm, "mid": v(58.99, -44.68) * mm, "end": v(60, -40.3) * mm});
            skArc(sketch, "E79.12", {"start": v(-56.15, -48.18) * mm, "mid": v(0, -67.5) * mm, "end": v(56.15, -48.18) * mm});
            skLineSegment(sketch, "E79.13", {"start": v(-60, 40.3) * mm, "end": v(-60, -40.3) * mm});
            skArc(sketch, "E79.14", {"start": v(-56.15, 48.18) * mm, "mid": v(-58.99, 44.68) * mm, "end": v(-60, 40.3) * mm});
            skArc(sketch, "E79.15", {"start": v(-60, -40.3) * mm, "mid": v(-58.99, -44.68) * mm, "end": v(-56.15, -48.18) * mm});
            skCircle(sketch, "E79.16", {"center": v(-60, 67.5) * mm, "radius": 4 * mm});
            skCircle(sketch, "E79.17", {"center": v(60, 67.5) * mm, "radius": 4 * mm});
            skCircle(sketch, "E79.18", {"center": v(60, -67.5) * mm, "radius": 4 * mm});
            skCircle(sketch, "E79.19", {"center": v(-60, -67.5) * mm, "radius": 4 * mm});
            skLineSegment(sketch, "E80", {"start": v(-33, 90) * mm, "end": v(-15, 108) * mm});
            skLineSegment(sketch, "E81", {"start": v(-15, 108) * mm, "end": v(-15, 120) * mm});
            skLineSegment(sketch, "E82", {"start": v(33, 90) * mm, "end": v(15, 108) * mm});
            skLineSegment(sketch, "E83", {"start": v(15, 108) * mm, "end": v(15, 120) * mm});
            skLineSegment(sketch, "E84", {"start": v(0, 90) * mm, "end": v(0, 120) * mm, "construction": true});
            skCircle(sketch, "E85", {"center": v(0, 120) * mm, "radius": 6 * mm});
            skArc(sketch, "E86", {"start": v(15, 120) * mm, "mid": v(0, 135) * mm, "end": v(-15, 120) * mm});
            skLineSegment(sketch, "E87", {"start": v(-57.24, 0) * mm, "end": v(81.5, 0) * mm, "construction": true});
            skPoint(sketch, "E87.endSnap0", {"position": v(80, 0) * mm});
            skLineSegment(sketch, "E88.MirrorCS", {"start": v(-33, -90) * mm, "end": v(-15, -108) * mm});
            skLineSegment(sketch, "E89.MirrorCS", {"start": v(-15, -108) * mm, "end": v(-15, -120) * mm});
            skArc(sketch, "E90.MirrorCS", {"start": v(-70, -90) * mm, "mid": v(-77.07, -87.07) * mm, "end": v(-80, -80) * mm});
            skLineSegment(sketch, "E91.MirrorCS", {"start": v(0, -90) * mm, "end": v(0, -120) * mm, "construction": true});
            skLineSegment(sketch, "E92.MirrorCS", {"start": v(15, -108) * mm, "end": v(15, -120) * mm});
            skArc(sketch, "E93.MirrorCS", {"start": v(80, -80) * mm, "mid": v(77.07, -87.07) * mm, "end": v(70, -90) * mm});
            skArc(sketch, "E94.MirrorCS", {"start": v(15, -120) * mm, "mid": v(0, -135) * mm, "end": v(-15, -120) * mm});
            skCircle(sketch, "E95.MirrorC", {"center": v(0, -120) * mm, "radius": 6 * mm});
            skLineSegment(sketch, "E96.MirrorCS", {"start": v(33, -90) * mm, "end": v(15, -108) * mm});
            skSolve(sketch);
        }
        {
            var Q0;
            Q0 = qSketchRegion(id + "F16", true);
            var Q1;
            Q1=makeQuery(id+"F2.opExtrude","CAP_FACE",FACE,{"disambiguationData":[OSD([sQuery(id+"F0.wireOp",EDGE,"E12"),sQuery(id+"F0.wireOp",EDGE,"E13"),sQuery(id+"F0.wireOp",EDGE,"E14"),sQuery(id+"F0.wireOp",EDGE,"E15"),sQuery(id+"F0.wireOp",EDGE,"E17.filletArc"),sQuery(id+"F0.wireOp",EDGE,"E18.filletArc"),sQuery(id+"F0.wireOp",EDGE,"E19.filletArc"),sQuery(id+"F0.wireOp",EDGE,"E20.filletArc"),sQuery(id+"F0.wireOp",EDGE,"E25.0"),sQuery(id+"F0.wireOp",EDGE,"E25.1"),sQuery(id+"F0.wireOp",EDGE,"E25.2"),sQuery(id+"F0.wireOp",EDGE,"E25.3"),sQuery(id+"F0.wireOp",EDGE,"E25.4"),sQuery(id+"F0.wireOp",EDGE,"E25.5"),sQuery(id+"F0.wireOp",EDGE,"E25.6"),sQuery(id+"F0.wireOp",EDGE,"E25.7")])],"isStart":false});
            extrude(context, id + "F17", {"entities" : qUnion([Q0]), "endBound" : BoundingType.UP_TO_SURFACE, "endBoundEntityFace" : qUnion([Q1]), "depth" : 25 * mm});
        }
    });
